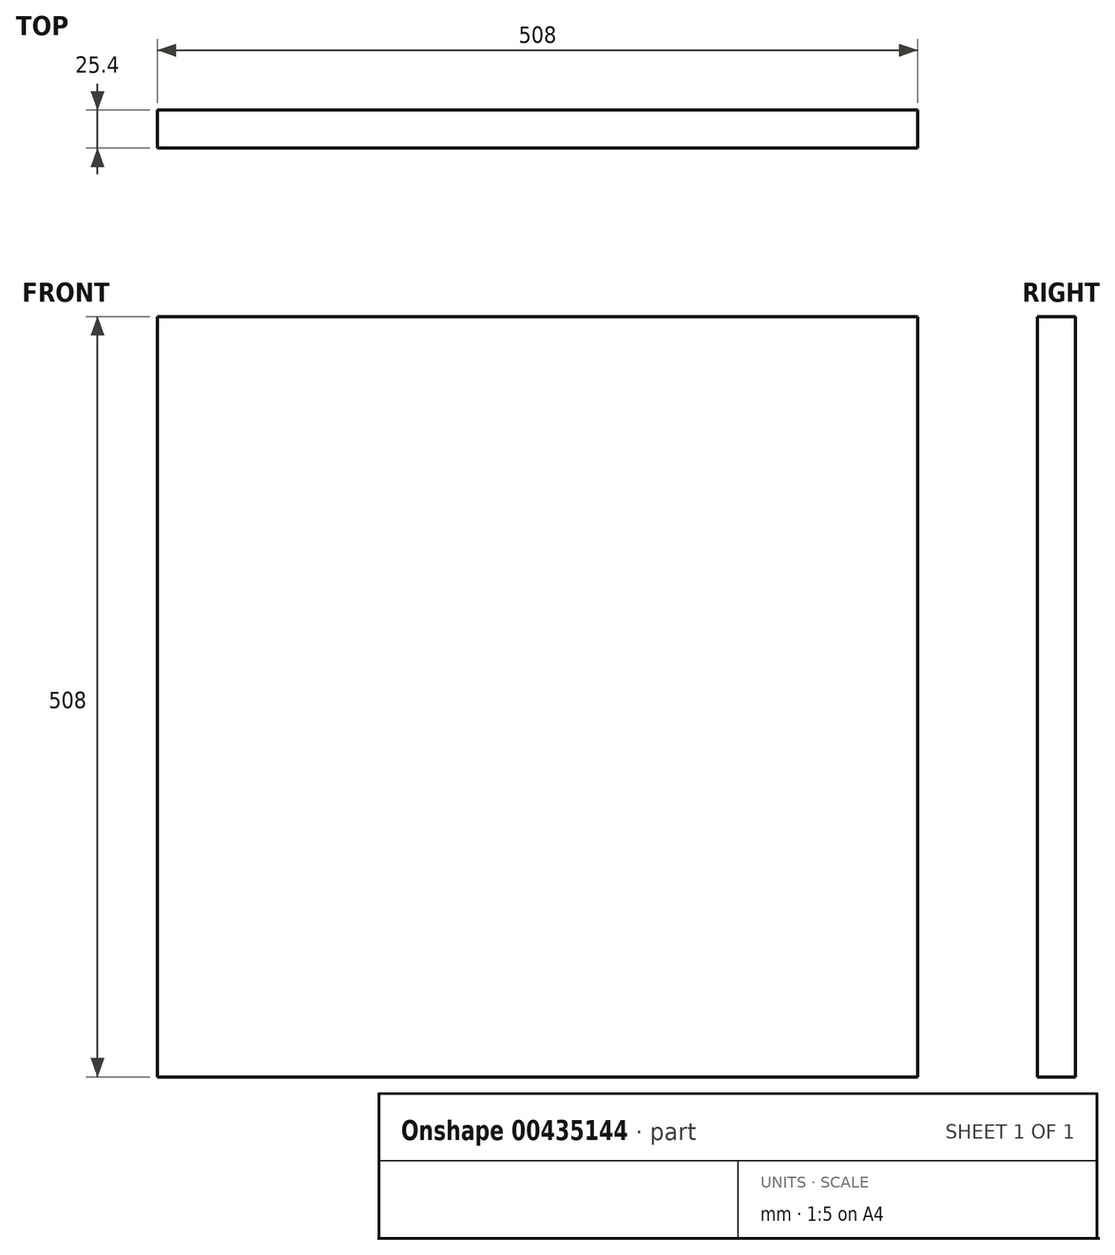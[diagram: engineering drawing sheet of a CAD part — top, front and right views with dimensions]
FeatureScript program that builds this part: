
annotation { "Feature Type Name" : "Feature", "Feature Type Description" : "" }
export const myFeature = defineFeature(function(context is Context, id is Id, definition is map)
    precondition{}
    {
        {
            var Q0;
            Q0=qCreatedBy(makeId("Front.planeOp"),FACE);
            var sketch = newSketch(context, id + "F0", { "sketchPlane" : qUnion([Q0])});
            skLineSegment(sketch, "E0.bottom", {"start": v(254, -254) * mm, "end": v(-254, -254) * mm});
            skLineSegment(sketch, "E0.top", {"start": v(254, 254) * mm, "end": v(-254, 254) * mm});
            skLineSegment(sketch, "E0.left", {"start": v(254, -254) * mm, "end": v(254, 254) * mm});
            skLineSegment(sketch, "E0.right", {"start": v(-254, -254) * mm, "end": v(-254, 254) * mm});
            skPoint(sketch, "E0.middle", {"position": v(0, 0) * mm});
            skSolve(sketch);
        }
        {
            var Q0;
            Q0=makeQuery(id+"F0.imprint","IMPRINT",FACE,{"disambiguationData":[TD([[makeQuery(id+"F0.imprint","IMPRINT",EDGE,{"derivedFrom":sQuery(id+"F0.wireOp",EDGE,"E0.bottom")}),-1.0]])]});
            extrude(context, id + "F1", {"entities" : qUnion([Q0]), "depth" : 25.4 * mm});
        }
    });
